# Revit family: pinhead
name_source: partatom
category: Allgemeines Modell
revit_build: Autodesk Revit 2018 (Build: 20190510_1515(x64)
units: mm (PartAtom-declared; Revit-internal decimal feet)

## family parameters
Arbeitsebenenbasiert = Ja
Beim Laden mit Abzugskörper schneiden = Ja
Bemaßung runder Anschluss = Durchmesser verwenden
Gemeinsam genutzt = Nein
Immer vertikal = Ja
Kann Basisbauteil für Bewehrung sein = Nein
Raumberechnungspunkt = Nein
Teiletyp = Normal

## types (3) — shared parameters
G_ = 130 mm
Geschossdecke_Staerke = 260 mm  [stored 0.853018 ft]
Schnittlinie = 3000 mm
Vorgabe-Ansicht = 1219 mm

## per-type parameters (varying)
| type | H_ | KB_ | KT_ | Kopfbreite | Kopfhoehe | Kopftiefe |
| 70x70 | 130 mm | 350 mm | 350 mm | 700 mm | 260 mm  [stored 0.853018 ft] | 700 mm |
| 60x60 | 125 mm | 300 mm | 300 mm | 600 mm | 250 mm | 600 mm |
| STB 26.0 70x70 | 130 mm | 350 mm | 350 mm | 700 mm | 260 mm  [stored 0.853018 ft] | 700 mm |

note: [stored X ft] marks values corroborated as IEEE doubles in the binary element streams (Revit-internal decimal feet)

## geometry (parser evidence)
native form markers: Blend x2
no freeform markers — native parametric forms only
